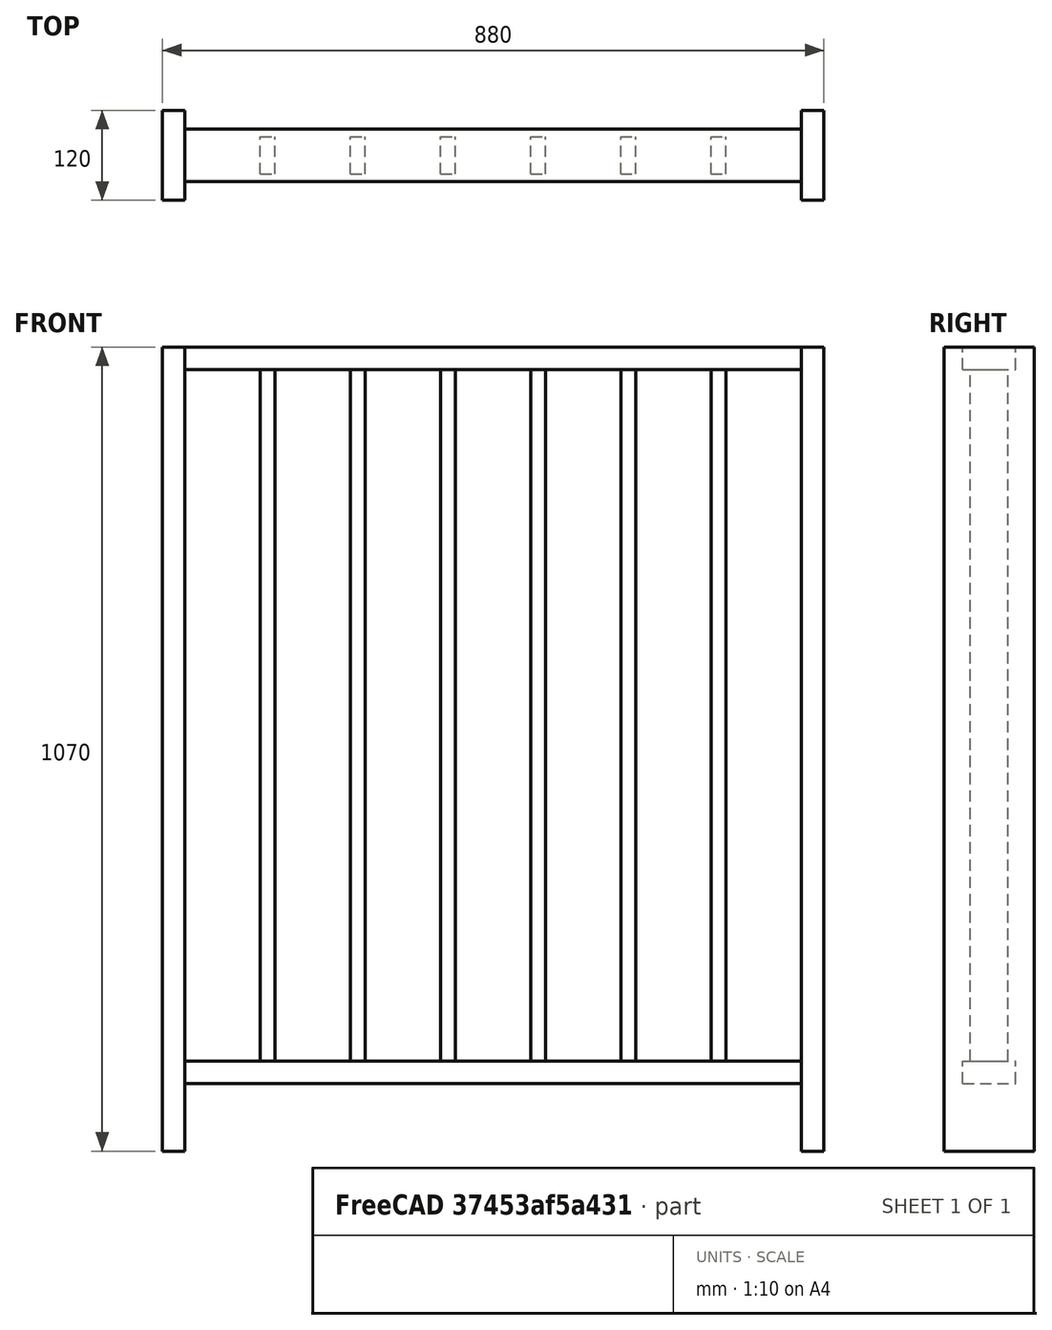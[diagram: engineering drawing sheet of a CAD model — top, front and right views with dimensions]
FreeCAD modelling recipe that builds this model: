
FCSTD DOCUMENT  (FreeCAD 0.18R16146 (Git))
Label: guarda-corpo-grade-modulo-1
License: All rights reserved
LicenseURL: http://en.wikipedia.org/wiki/All_rights_reserved
objects: Part::Box×5, Spreadsheet::Sheet×1, Part::FeaturePython×1, Part::Compound×1, Part::Feature×1
note: 8 computed .brp shape members not serialized (recipe doc carries the construction recipe); baked Part::Feature solids carry a one-line shape summary decoded from their .brp

FEATURE [Spreadsheet::Sheet] Spreadsheet  label="medidas"
  cells = B1=altura (height); C1=frente (length); D1=profundidade (width); E1=z; F1=x; G1=y; H1=quantidade; A2=pe_direito_1; B2(pe_direito_1_height)=1070; C2(pe_direito_1_length)=30; D2(pe_direito_1_width)=120; E2(pe_direito_1_z)=0; F2(pe_direito_1_x)=0; G2(pe_direito_1_y)=0; H2=1; A3=pe_direito_2; B3(pe_direito_2_height)=1070; C3(pe_direito_2_length)=30; D3(pe_direito_2_width)=120; E3(pe_direito_2_z)=0; F3(pe_direito_2_x)=850; G3(pe_direito_2_y)=0; H3=1; A4=travessa_inferior; B4(travessa_inferior_height)=30; C4(travessa_inferior_length)=820; D4(travessa_inferior_width)=70; E4(travessa_inferior_z)=90; F4(travessa_inferior_x)=30; G4(travessa_inferior_y)=25; H4=1; A5=travessa_superior; B5(travessa_superior_height)=30; C5(travessa_superior_length)=820; D5(travessa_superior_width)=70; E5(travessa_superior_z)=1040; F5(travessa_superior_x)=30; G5(travessa_superior_y)=25; H5=1; A6=palito_grade; B6(palito_grade_height)=920; C6(palito_grade_length)=20; D6(palito_grade_width)=50; E6(palito_grade_z)=0; F6(palito_grade_x)=0; G6(palito_grade_y)=0; H6=1; A7=palitos; C7(palitos_length)=120; E7(palitos_z)=120; F7(palitos_x)=130; G7(palitos_y)=35; H7(palitos_qty)=6
FEATURE [Part::Box] Box  label="pe_direito_1"
  AttacherType = Attacher::AttachEngine3D
  Height = 1070
  Length = 30
  Width = 120
  expr: Placement.Base.z = medidas.pe_direito_1_z
  expr: Placement.Base.y = medidas.pe_direito_1_y
  expr: Placement.Base.x = medidas.pe_direito_1_x
  expr: Height = medidas.pe_direito_1_height
  expr: Width = medidas.pe_direito_1_width
  expr: Length = medidas.pe_direito_1_length
FEATURE [Part::Box] Box001  label="pe_direito_2"
  AttacherType = Attacher::AttachEngine3D
  Height = 1070
  Length = 30
  Placement = pos=(850,0,0) rot=(0,0,1;0rad)
  Width = 120
  expr: Placement.Base.z = medidas.pe_direito_2_z
  expr: Placement.Base.y = medidas.pe_direito_2_y
  expr: Placement.Base.x = medidas.pe_direito_2_x
  expr: Height = medidas.pe_direito_2_height
  expr: Width = medidas.pe_direito_2_width
  expr: Length = medidas.pe_direito_2_length
FEATURE [Part::Box] Box002  label="travessa_inferior"
  AttacherType = Attacher::AttachEngine3D
  Height = 30
  Length = 820
  Placement = pos=(30,25,90) rot=(0,0,1;0rad)
  Width = 70
  expr: Placement.Base.z = medidas.travessa_inferior_z
  expr: Placement.Base.y = medidas.travessa_inferior_y
  expr: Placement.Base.x = medidas.travessa_inferior_x
  expr: Height = medidas.travessa_inferior_height
  expr: Width = medidas.travessa_inferior_width
  expr: Length = medidas.travessa_inferior_length
FEATURE [Part::Box] Box003  label="travessa_superior"
  AttacherType = Attacher::AttachEngine3D
  Height = 30
  Length = 820
  Placement = pos=(30,25,1040) rot=(0,0,1;0rad)
  Width = 70
  expr: Placement.Base.z = medidas.travessa_superior_z
  expr: Placement.Base.y = medidas.travessa_superior_y
  expr: Placement.Base.x = medidas.travessa_superior_x
  expr: Height = medidas.travessa_superior_height
  expr: Width = medidas.travessa_superior_width
  expr: Length = medidas.travessa_superior_length
FEATURE [Part::Box] Box004  label="palito_grade"
  AttacherType = Attacher::AttachEngine3D
  Height = 920
  Length = 20
  Width = 50
  expr: Placement.Base.z = medidas.palito_grade_z
  expr: Placement.Base.y = medidas.palito_grade_y
  expr: Placement.Base.x = medidas.palito_grade_x
  expr: Height = medidas.palito_grade_height
  expr: Width = medidas.palito_grade_width
  expr: Length = medidas.palito_grade_length
FEATURE [Part::FeaturePython] Array  label="palitos"  # Draft array (typed FeaturePython)
  Angle = 360
  ArrayType = 0
  Axis = (0,0,1)
  Base = -> Box004
  Center = (0,0,0)
  Fuse = false
  IntervalAxis = (0,0,0)
  IntervalX = (120,0,0)
  IntervalY = (0,1,0)
  IntervalZ = (0,0,1)
  NumberPolar = 1
  NumberX = 6
  NumberY = 1
  NumberZ = 1
  Placement = pos=(130,35,120) rot=(0,0,1;0rad)
  expr: IntervalX.x = medidas.palitos_length
  expr: NumberX = medidas.palitos_qty
  expr: Placement.Base.z = medidas.palitos_z
  expr: Placement.Base.y = medidas.palitos_y
  expr: Placement.Base.x = medidas.palitos_x
FEATURE [Part::Compound] Compound  label="modulo_1"
  Links = -> [Box,Box001,Box002,Box003,Array]
FEATURE [Part::Feature] Compound001  label="modulo_1_copy"
  shape: bbox 880 x 120 x 1070 mm, 60 faces, 10 solids (baked)
